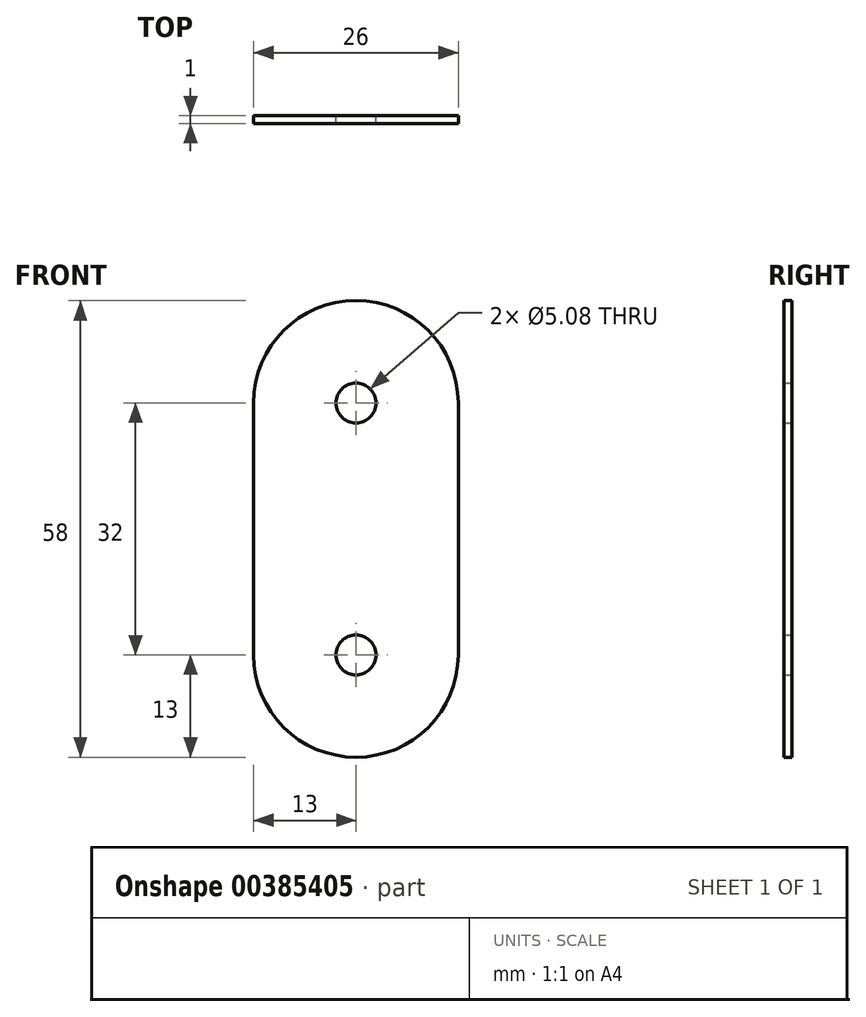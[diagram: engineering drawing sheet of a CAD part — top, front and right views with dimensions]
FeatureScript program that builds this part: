
annotation { "Feature Type Name" : "Feature", "Feature Type Description" : "" }
export const myFeature = defineFeature(function(context is Context, id is Id, definition is map)
    precondition{}
    {
        {
            var Q0;
            Q0=qCreatedBy(makeId("Front.planeOp"),FACE);
            var sketch = newSketch(context, id + "F0", { "sketchPlane" : qUnion([Q0])});
            skLineSegment(sketch, "E0", {"start": v(-13, 16) * mm, "end": v(-13, -16) * mm});
            skLineSegment(sketch, "E1", {"start": v(13, -16) * mm, "end": v(13, 16) * mm});
            skCircle(sketch, "E2", {"center": v(0, 16) * mm, "radius": 2.54 * mm});
            skCircle(sketch, "E3", {"center": v(0, -16) * mm, "radius": 2.54 * mm});
            skCircle(sketch, "E4", {"center": v(0, 16) * mm, "radius": 13 * mm});
            skCircle(sketch, "E5", {"center": v(0, -16) * mm, "radius": 13 * mm});
            skSolve(sketch);
        }
        {
            var Q0;
            Q0=qSketchRegion(id+"F0",true);
            extrude(context, id + "F1", {"entities" : qUnion([Q0]), "depth" : 1 * mm});
        }
    });
